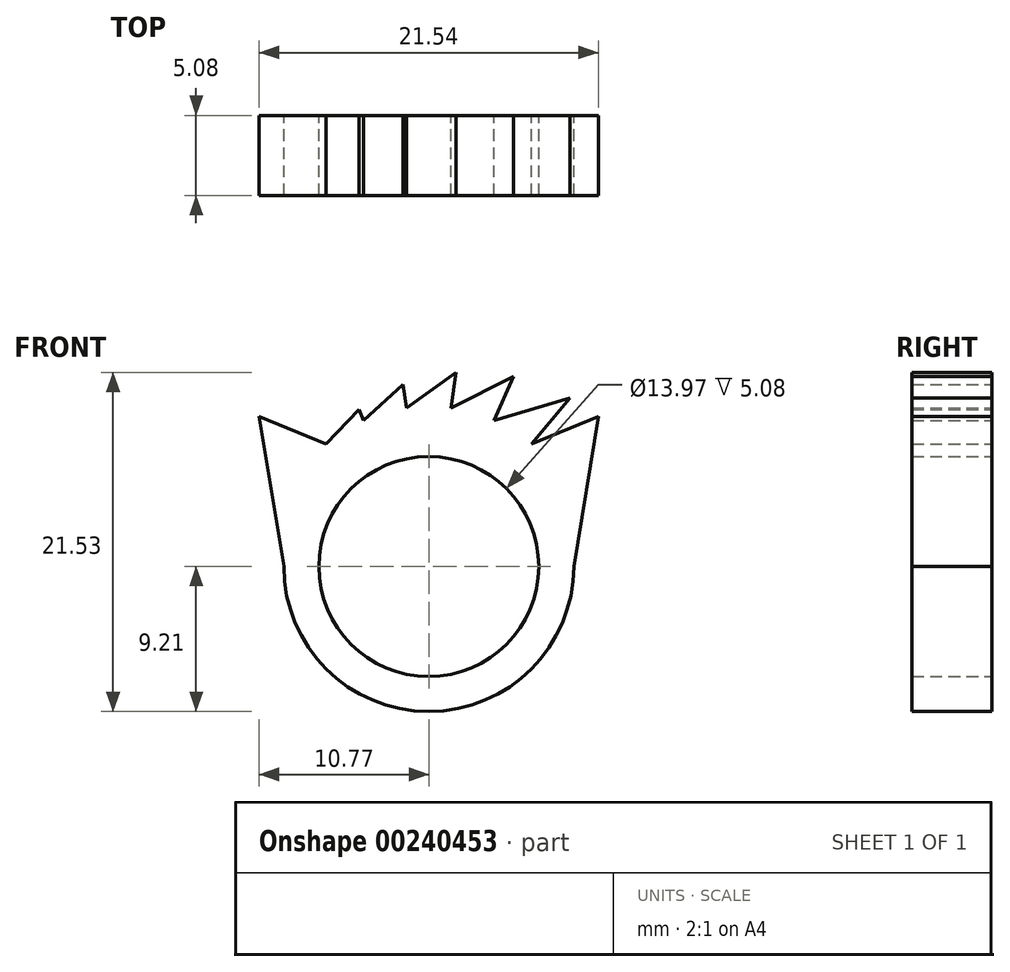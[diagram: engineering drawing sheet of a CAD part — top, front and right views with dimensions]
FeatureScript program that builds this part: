
annotation { "Feature Type Name" : "Feature", "Feature Type Description" : "" }
export const myFeature = defineFeature(function(context is Context, id is Id, definition is map)
    precondition{}
    {
        {
            var Q0;
            Q0=qCreatedBy(makeId("Front.planeOp"),FACE);
            var sketch = newSketch(context, id + "F0", { "sketchPlane" : qUnion([Q0])});
            skCircle(sketch, "E0", {"center": v(0, 0) * mm, "radius": 6.99 * mm});
            skCircle(sketch, "E1", {"center": v(0, 0) * mm, "radius": 9.2 * mm});
            skLineSegment(sketch, "E2", {"start": v(-9.2, 0) * mm, "end": v(-10.36, 6.99) * mm});
            skLineSegment(sketch, "E3", {"start": v(9.2, 0) * mm, "end": v(10.36, 6.99) * mm});
            skLineSegment(sketch, "E4", {"start": v(-6.53, 7.78) * mm, "end": v(-4.44, 9.98) * mm});
            skLineSegment(sketch, "E5", {"start": v(-4.44, 9.98) * mm, "end": v(-4.13, 9.28) * mm});
            skLineSegment(sketch, "E6", {"start": v(-4.13, 9.28) * mm, "end": v(-1.63, 11.57) * mm});
            skLineSegment(sketch, "E7", {"start": v(-1.63, 11.57) * mm, "end": v(-1.41, 10.06) * mm});
            skLineSegment(sketch, "E8", {"start": v(1.41, 10.06) * mm, "end": v(5.37, 12.07) * mm});
            skLineSegment(sketch, "E9", {"start": v(5.37, 12.07) * mm, "end": v(4.13, 9.28) * mm});
            skLineSegment(sketch, "E10", {"start": v(4.13, 9.28) * mm, "end": v(8.98, 10.7) * mm});
            skLineSegment(sketch, "E11", {"start": v(8.98, 10.7) * mm, "end": v(6.53, 7.78) * mm});
            skLineSegment(sketch, "E12", {"start": v(6.53, 7.78) * mm, "end": v(10.77, 9.53) * mm});
            skLineSegment(sketch, "E13", {"start": v(10.77, 9.53) * mm, "end": v(10.36, 6.99) * mm});
            skCircle(sketch, "E14", {"center": v(0, 0) * mm, "radius": 10.16 * mm, "construction": true});
            skLineSegment(sketch, "E15", {"start": v(0, 0) * mm, "end": v(-6.53, 7.78) * mm, "construction": true});
            skLineSegment(sketch, "E16", {"start": v(0, 0) * mm, "end": v(-4.13, 9.28) * mm, "construction": true});
            skLineSegment(sketch, "E17", {"start": v(0, 0) * mm, "end": v(-1.41, 10.06) * mm, "construction": true});
            skLineSegment(sketch, "E18", {"start": v(1.41, 10.06) * mm, "end": v(0, 0) * mm, "construction": true});
            skLineSegment(sketch, "E19", {"start": v(4.13, 9.28) * mm, "end": v(0, 0) * mm, "construction": true});
            skLineSegment(sketch, "E20", {"start": v(6.53, 7.78) * mm, "end": v(0, 0) * mm, "construction": true});
            skLineSegment(sketch, "E21", {"start": v(0, 0) * mm, "end": v(10.36, 6.99) * mm, "construction": true});
            skLineSegment(sketch, "E22", {"start": v(0, 0) * mm, "end": v(-10.36, 6.99) * mm, "construction": true});
            skLineSegment(sketch, "E23", {"start": v(0, 0) * mm, "end": v(0, 16.42) * mm, "construction": true});
            skLineSegment(sketch, "E24", {"start": v(-1.41, 10.06) * mm, "end": v(1.73, 12.32) * mm});
            skLineSegment(sketch, "E25", {"start": v(1.73, 12.32) * mm, "end": v(1.41, 10.06) * mm});
            skLineSegment(sketch, "E26", {"start": v(-10.36, 6.99) * mm, "end": v(-10.77, 9.53) * mm});
            skLineSegment(sketch, "E27", {"start": v(-6.53, 7.78) * mm, "end": v(-10.77, 9.53) * mm});
            skSolve(sketch);
        }
        {
            var Q0;
            {var subQ1=sQuery(id+"F0.wireOp",EDGE,"E2");Q0=makeQuery(id+"F0.imprint","IMPRINT",FACE,{"disambiguationData":[TD([[makeQuery(id+"F0.imprint","IMPRINT",EDGE,{"derivedFrom":subQ1}),-1.0]])]});}
            var Q1;
            Q1=makeQuery(id+"F0.imprint","IMPRINT",FACE,{"disambiguationData":[TD([[makeQuery(id+"F0.imprint","IMPRINT",EDGE,{"derivedFrom":sQuery(id+"F0.wireOp",EDGE,"E0")}),-1.0]])]});
            extrude(context, id + "F1", {"entities" : qUnion([Q0, Q1]), "depth" : 5.08 * mm});
        }
    });
